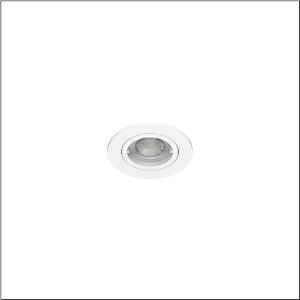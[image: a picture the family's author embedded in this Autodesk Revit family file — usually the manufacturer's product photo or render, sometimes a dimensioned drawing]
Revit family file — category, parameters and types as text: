
# Revit family: lunis_41_spot_51dt137a42a
name_source: partatom
category: Lighting Fixtures
units: mm (PartAtom-declared; Revit-internal decimal feet)

## family parameters
Cut with Voids When Loaded = No
Host = Face
Light Source = No
Part Type = Normal
Room Calculation Point = No
Round Connector Dimension = Use Diameter
Shared = No

## types (1)
- Lunis 41 Spot (1 x LED, 720 lm, 6.5 W, 4000K)
    Apparent Load = 7 VA
    CIE Flux Codes = 87 97 99 100 100
    Color Rendering = 80
    Color Temperature = 4000K
    Default Elevation = 1800 mm
    Description = Lunis 41,  Spot, downlight, light emission: direct distribution, LED rated luminous flux: 720lm, light colour: 840, control gear: ECG, mains connection: 230V, AC, 50/60Hz, housing, round, of aluminium, coated, traffic white (RAL 9016), diameter: 88mm, recess depth: 54mm, protection rating (complete): IP20, protection rating (on room side): IP20, insulation class (complete): insulation class II (safety insulation), certification: CE, permissible ambient temperature for indoor applications: -20..+40°C, packaging unit: 1 piece
    Height = 0 mm  [stored 0 ft]
    Lamp = 1 x LED
    Lamp Light Flux = 720 lm
    Lamp Power = 6.5 W
    Lamp count = 1
    Length = 88 mm
    Luminous efficacy = 111 lm/W
    Manufacturer = Siteco
    ModVariant = No
    Model = 51DT137A42A
    Mounting Place = Ceiling
    Mounting Type = Recessed
    Number of Poles = 1
    OnlyDefault = Yes
    Power Factor = 1
    Product Name = Lunis 41 Spot
    Product group = downlight
    ProductGroupID = 400
    Protection Class = Protection class II
    Protection Degree = IP 20
    RLX_Detail_Level = 1
    RLX_Emergency_Light_Flux = 0 lm
    RLX_Emergency_Type = 0
    RLX_Emergency_Type_DB = No
    RlxData = <blob elided: 38045 chars, md5=96566a0b>
    Socket = socket
    Standby Power = 0 W
    System Light Flux = 720 lm
    System Power = 7 W
    Type Comments = Product without accessories
    Type Image = l_1005286.jpg
    URL = http://relux.com
    VarID = ---
    Voltage = 0 V
    Weight = 0.00 kg
    Width = 0 mm  [stored 0 ft]

note: [stored X ft] marks values corroborated as IEEE doubles in the binary element streams (Revit-internal decimal feet)

## geometry (parser evidence)
native form markers: Blend x4, Sweep x9
no freeform markers — native parametric forms only
